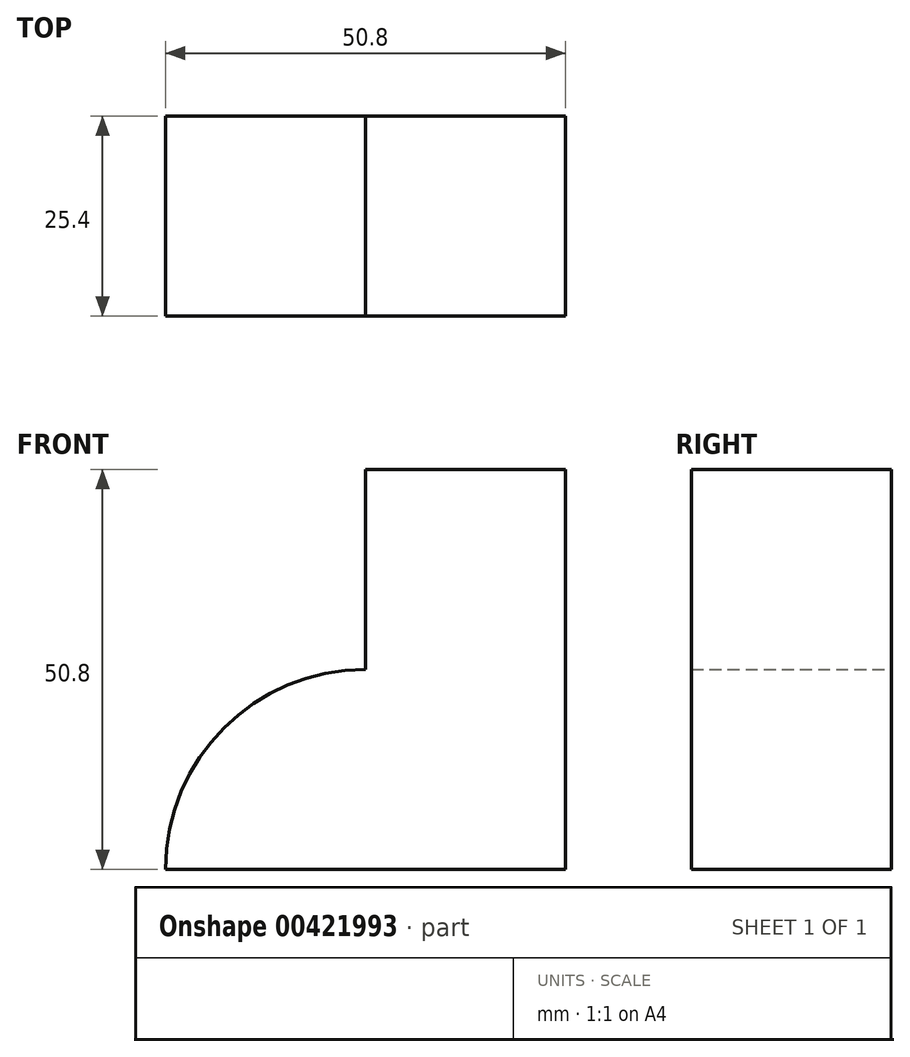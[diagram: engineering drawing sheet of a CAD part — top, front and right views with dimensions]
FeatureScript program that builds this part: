
annotation { "Feature Type Name" : "Feature", "Feature Type Description" : "" }
export const myFeature = defineFeature(function(context is Context, id is Id, definition is map)
    precondition{}
    {
        {
            var Q0;
            Q0=qCreatedBy(makeId("Front.planeOp"),FACE);
            var sketch = newSketch(context, id + "F0", { "sketchPlane" : qUnion([Q0])});
            skLineSegment(sketch, "E0", {"start": v(0, 0) * mm, "end": v(0, 50.8) * mm});
            skLineSegment(sketch, "E1", {"start": v(0, 50.8) * mm, "end": v(-25.4, 50.8) * mm});
            skLineSegment(sketch, "E2", {"start": v(-25.4, 50.8) * mm, "end": v(-25.4, 25.4) * mm});
            skLineSegment(sketch, "E3", {"start": v(0, 0) * mm, "end": v(-50.8, 0) * mm});
            skArc(sketch, "E4", {"start": v(-25.4, 25.4) * mm, "mid": v(-43.36, 17.96) * mm, "end": v(-50.8, 0) * mm});
            skSolve(sketch);
        }
        {
            var Q0;
            Q0 = qSketchRegion(id + "F0", true);
            extrude(context, id + "F1", {"entities" : qUnion([Q0]), "depth" : 25.4 * mm});
        }
    });
